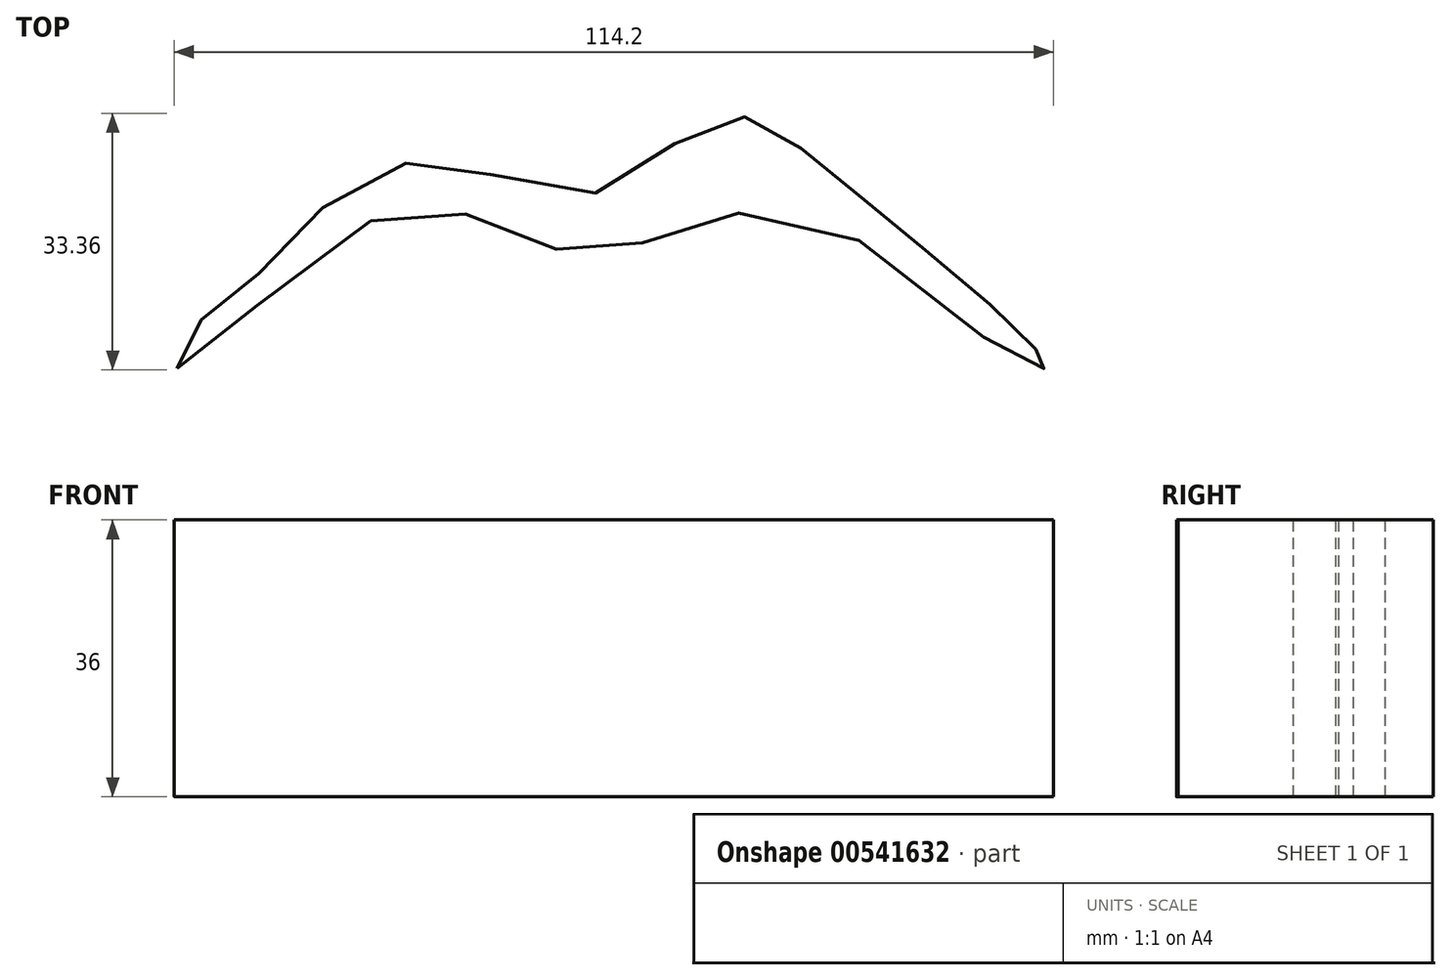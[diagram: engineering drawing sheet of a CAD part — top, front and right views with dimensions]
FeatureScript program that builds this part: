
annotation { "Feature Type Name" : "Feature", "Feature Type Description" : "" }
export const myFeature = defineFeature(function(context is Context, id is Id, definition is map)
    precondition{}
    {
        {
            var Q0;
            Q0=qCreatedBy(makeId("Top.planeOp"),FACE);
            var sketch = newSketch(context, id + "F0", { "sketchPlane" : qUnion([Q0])});
            skFitSpline(sketch, "E0", {"points": [v(-51.23, 0) * mm, v(-50.3, 4.05) * mm, v(-43.78, 9.27) * mm, v(-35.58, 17.93) * mm, v(-22.47, 26.45) * mm, v(-10.25, 25.12) * mm, v(7.44, 23.84) * mm, v(17.93, 32.86) * mm, v(26.79, 30.67) * mm, v(31.07, 27.63) * mm, v(39.82, 20.5) * mm, v(48.56, 13.26) * mm, v(57.7, 5.28) * mm, v(60.98, 1.82) * mm, v(62.62, 0) * mm, v(61.5, 0) * mm, v(59.2, 0) * mm, v(33.1, 18.84) * mm, v(13.05, 17.67) * mm, v(0, 15.06) * mm, v(-14.74, 20.36) * mm, v(-31.93, 15.69) * mm, v(-51.23, 0) * mm]});
            skSolve(sketch);
        }
        {
            var Q0;
            Q0=makeQuery(id+"F0.imprint","IMPRINT",FACE,{"disambiguationData":[TD([[makeQuery(id+"F0.imprint","IMPRINT",EDGE,{"derivedFrom":sQuery(id+"F0.wireOp",EDGE,"E0")}),-1.0]])]});
            extrude(context, id + "F1", {"entities" : qUnion([Q0]), "depth" : 36 * mm, "offsetDistance" : 25 * mm});
        }
    });
